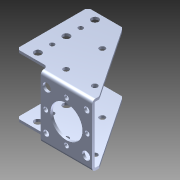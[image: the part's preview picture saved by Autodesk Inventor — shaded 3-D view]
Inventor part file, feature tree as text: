
AUTODESK INVENTOR PART (.ipt)
format: ipt  version: 2015 SP1 (Build 190203100, 203)  size: 218,112 bytes
history: native  units: in
note: dims shown in document units (in); Inventor stores cm internally (conversion verified against a paired STEP export)
features: other x2, extrude x1, imported_body x1, sketch x1
ambient origin geometry x8: Origin, YZ Plane, XZ Plane, XY Plane, X Axis, Y Axis, Z Axis, Center Point
bodies: Body1 (feature_tree)
feature tree (5):
  other  "Cut-Extrude6"
  other  "2in horizontal gearbox mount1"
  extrude  "Extrusion1"  Depth=0.25in
  imported_body  "Base1"
  sketch  "Sketch1"  dims[d0=0.25in d1=0.25in d2=0.25in d3=3.0in d4=0.0in]
